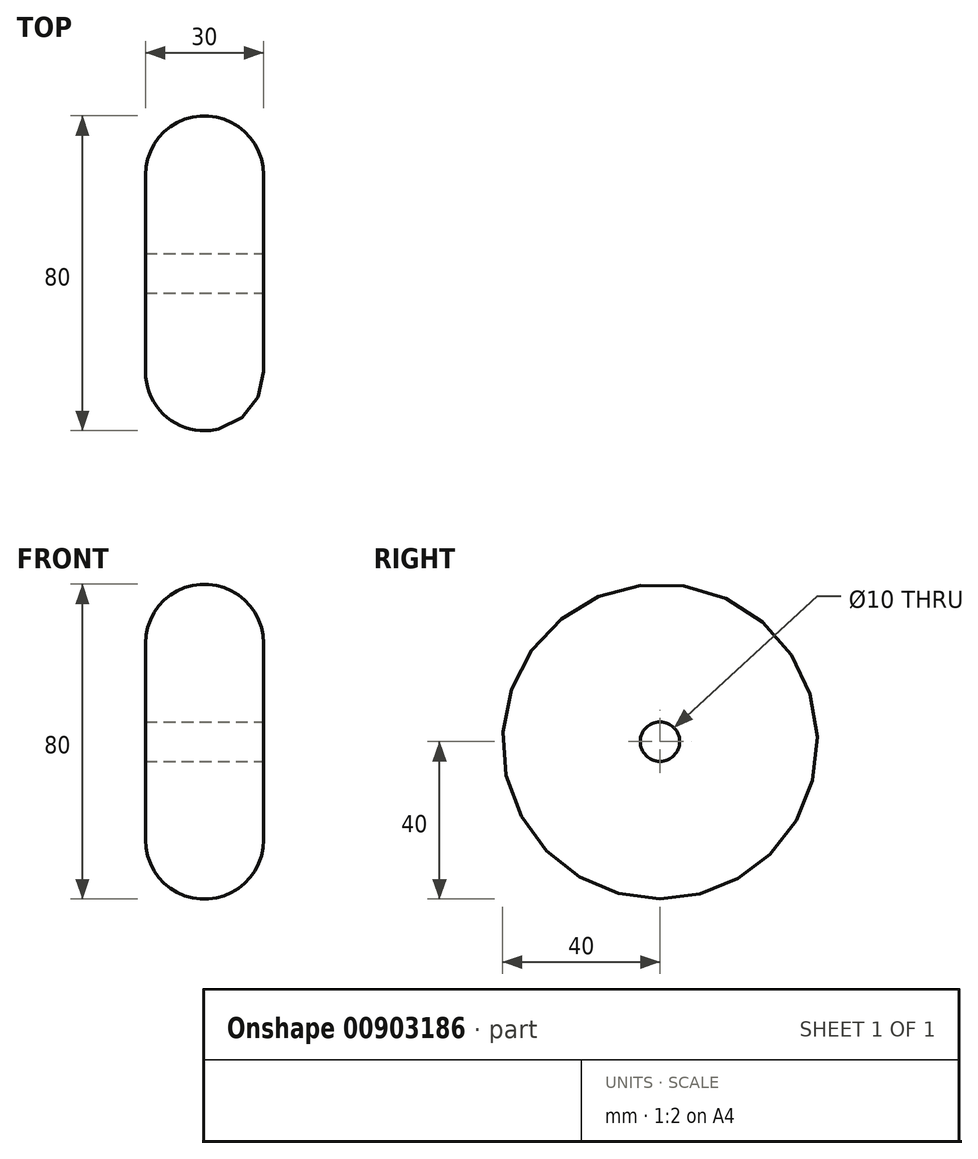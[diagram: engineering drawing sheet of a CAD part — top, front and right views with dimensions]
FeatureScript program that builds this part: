
annotation { "Feature Type Name" : "Feature", "Feature Type Description" : "" }
export const myFeature = defineFeature(function(context is Context, id is Id, definition is map)
    precondition{}
    {
        {
            var Q0;
            Q0=qCreatedBy(makeId("Front.planeOp"),FACE);
            var sketch = newSketch(context, id + "F0", { "sketchPlane" : qUnion([Q0])});
            skArc(sketch, "E0", {"start": v(15, 0) * mm, "mid": v(0, 15) * mm, "end": v(-15, 0) * mm});
            skLineSegment(sketch, "E1", {"start": v(-15, 0) * mm, "end": v(-15, -20) * mm});
            skLineSegment(sketch, "E2", {"start": v(15, -20) * mm, "end": v(15, 0) * mm});
            skLineSegment(sketch, "E3", {"start": v(0, 0) * mm, "end": v(0, -25) * mm, "construction": true});
            skLineSegment(sketch, "E4", {"start": v(0, -25) * mm, "end": v(-50, -25) * mm, "construction": true});
            skLineSegment(sketch, "E5", {"start": v(0, -25) * mm, "end": v(-15, -25) * mm});
            skLineSegment(sketch, "E6.0", {"start": v(15, -20) * mm, "end": v(-15, -20) * mm});
            skSolve(sketch);
        }
        {
            var Q0;
            Q0=makeQuery(id+"F0.imprint","IMPRINT",FACE,{"disambiguationData":[TD([[makeQuery(id+"F0.imprint","IMPRINT",EDGE,{"derivedFrom":sQuery(id+"F0.wireOp",EDGE,"E0")}),1.0]])]});
            var Q1;
            Q1=sQuery(id+"F0.wireOp",EDGE,"E4");
            revolve(context, id + "F1", {"surfaceOperationType" : NewSurfaceOperationType.NEW, "entities" : qUnion([Q0]), "axis" : qUnion([Q1]), "revolveType" : RevolveType.FULL});
        }
    });
